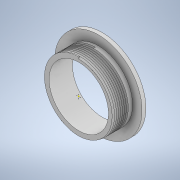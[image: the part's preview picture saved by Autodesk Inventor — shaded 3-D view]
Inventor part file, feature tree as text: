
AUTODESK INVENTOR PART (.ipt)
format: ipt  version: 2022.2 (Build 262287030, 287C)  size: 273,920 bytes
history: native  units: in
note: dims shown in document units (in); Inventor stores cm internally (conversion verified against a paired STEP export)
features: sketch x4, extrude x2, plane x1, helix x1
ambient origin geometry x8: Origin, YZ Plane, XZ Plane, XY Plane, X Axis, Y Axis, Z Axis, Center Point
bodies: Solid1 (feature_tree)
feature tree (8):
  extrude  "Extrusion1"  Depth=1.7614in
  extrude  "Extrusion2"  Depth=1.3831in
  sketch  "Sketch3"  dims[d7=0.0in]
  plane  "Work Plane1"
  helix  "Coil1"  [1 undecoded]
  sketch  "Sketch1"  dims[d0=1.1969in d1=1.7614in]
  sketch  "Sketch2"  dims[d2=0.0787in d3=0.0in d4=1.3831in d5=0.3937in d6=0.0in]
  sketch  "Sketch4"  dims[d8=0.0in d9=0.0in d10=0.0394in d11=0.0394in d12=0.3937in d13=3.1496in d14=0.0in d15=90.0deg d16=90.0deg d17=0.0in d18=0.0in d19=0.0401in]
note: 1 required parameter value undecoded (feature->parameter linkage not recoverable at this tier; creation-order binding heuristic only, values carry confidence <= 0.55)
